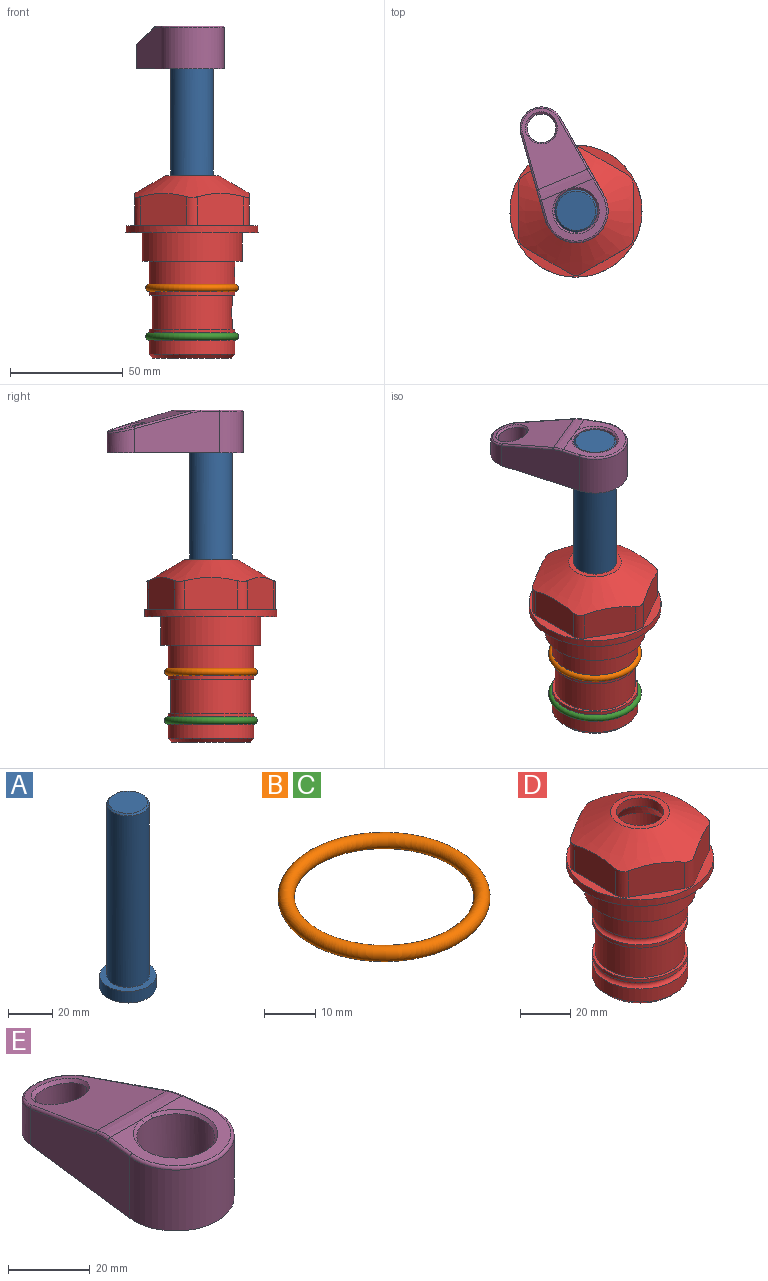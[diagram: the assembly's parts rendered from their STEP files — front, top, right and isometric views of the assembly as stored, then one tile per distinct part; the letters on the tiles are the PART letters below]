
ASSEMBLY  parts=5 mates=4
PART A: 6 faces, bbox 25.4x25.4x101.6 mm
  f0: plane 17.46x17.46mm, normal (0,0,1), area 239.5mm2, adj f5
  f1: plane 25.4x25.4mm, normal (0,0,-1), area 506.7mm2, adj f2
  f2: cylinder r=12.7mm len=25.4mm, axis (0,0,1), area 506.7mm2, adj f1,f3
  f3: plane 25.4x25.4mm, normal (0,0,1), area 221.7mm2, adj f2,f4
  f4: cylinder r=9.53mm len=94.46mm, axis (0,0,1), area 5653mm2, adj f3,f5
  f5: cone r=8.73mm half-angle=45deg, axis (0,0,-1), area 64.4mm2, adj f0,f4
PART B: 1 faces, bbox 44.7x44.7x3.2 mm
  f0: torus R=19.05mm, axis (0,0,1), area 1193.9mm2
PART C: same geometry as B
PART D: 36 faces, bbox 58.7x58.7x81 mm
  f0: cylinder r=17.78mm len=35.56mm, axis (0,0,1), area 1670.8mm2, adj f23,f24,f31
  f1: cylinder r=19.05mm len=38.1mm, axis (0,0,1), area 1191.9mm2, adj f26,f27,f30
  f2: plane 58.66x58.66mm, normal (0,0,-1), area 1150.6mm2, adj f3,f28
  f3: cylinder r=29.33mm len=58.66mm, axis (0,0,-1), area 585.1mm2, adj f2,f4
  f4: plane 58.66x58.66mm, normal (0,0,1), area 475.9mm2, adj f3,f5,f6,f7,f8,f9,f10,f11
  f5: plane 20.32x14.34mm, normal (-0.5,0.87,0), area 324.4mm2, adj f4,f15,f16,f17
  f6: plane 20.32x14.34mm, normal (0.5,0.87,0), area 324.4mm2, adj f4,f14,f15,f17
  f7: plane 23.48x14.34mm, normal (1,0,0), area 324.4mm2, adj f4,f13,f14,f17
  f8: plane 20.32x14.34mm, normal (0.5,-0.87,0), area 324.4mm2, adj f4,f12,f13,f17
  f9: plane 20.32x14.34mm, normal (-0.5,-0.87,0), area 324.4mm2, adj f4,f11,f12,f17
  f10: plane 23.48x14.34mm, normal (-1,0,0), area 324.4mm2, adj f4,f11,f16,f17
  f11: cylinder r=5.08mm len=12.85mm, axis (0,0,-1), area 67.2mm2, adj f4,f9,f10,f17
  f12: cylinder r=5.08mm len=12.85mm, axis (0,0,-1), area 67.2mm2, adj f4,f8,f9,f17
  f13: cylinder r=5.08mm len=12.85mm, axis (0,0,-1), area 67.2mm2, adj f4,f7,f8,f17
  f14: cylinder r=5.08mm len=12.85mm, axis (0,0,-1), area 67.2mm2, adj f4,f6,f7,f17
  f15: cylinder r=5.08mm len=12.85mm, axis (0,0,-1), area 67.2mm2, adj f4,f5,f6,f17
  f16: cylinder r=5.08mm len=12.85mm, axis (0,0,-1), area 67.2mm2, adj f4,f5,f10,f17
  f17: cone r=11.73mm half-angle=60deg, axis (0,0,-1), area 2071.8mm2, adj f5,f6,f7,f8,f9,f10,f11,f12
  f18: plane 23.46x23.46mm, normal (0,0,1), area 147.4mm2, adj f17,f35
  f19: plane 34.93x34.93mm, normal (0,0,-1), area 958mm2, adj f29
  f20: cylinder r=19.05mm len=38.1mm, axis (0,0,1), area 760.1mm2, adj f21,f29
  f21: torus R=19.05mm, axis (0,0,1), area 565.3mm2, adj f20,f22
  f22: cylinder r=19.05mm len=38.1mm, axis (0,0,1), area 190mm2, adj f21,f23
  f23: plane 38.1x38.1mm, normal (0,0,1), area 146.9mm2, adj f0,f22
  f24: plane 38.1x38.1mm, normal (0,0,-1), area 146.9mm2, adj f0,f25
  f25: cylinder r=19.05mm len=38.1mm, axis (0,0,1), area 190mm2, adj f24,f26
  f26: torus R=19.05mm, axis (0,0,1), area 565.3mm2, adj f1,f25
  f27: plane 44.45x44.45mm, normal (0,0,-1), area 411.7mm2, adj f1,f28
  f28: cylinder r=22.23mm len=44.45mm, axis (0,0,1), area 1773.5mm2, adj f2,f27
  f29: cone r=19.05mm half-angle=45deg, axis (0,0,1), area 257.5mm2, adj f19,f20
  f30: cylinder r=3.17mm len=6.75mm, axis (-1,0,0), area 128mm2, adj f1,f33
  f31: cylinder r=3.17mm len=6.35mm, axis (-1,0,0), area 102.5mm2, adj f0,f33
  f32: plane 25.4x25.4mm, normal (0,0,1), area 506.7mm2, adj f33
  f33: cylinder r=12.7mm len=66.42mm, axis (0,0,-1), area 5236.2mm2, adj f30,f31,f32,f34
  f34: cone r=9.53mm half-angle=30deg, axis (0,0,-1), area 443.4mm2, adj f33,f35
  f35: cylinder r=9.53mm len=19.05mm, axis (0,0,-1), area 240.9mm2, adj f18,f34
PART E: 31 faces, bbox 31.7x65.5x19.8 mm
  f0: plane 39.12x18.26mm, normal (0.99,0.12,0), area 612.2mm2, adj f1,f4,f7,f11,f13,f15
  f1: cylinder r=9.53mm len=18.91mm, axis (0,0,-1), area 296.1mm2, adj f0,f2,f7,f17
  f2: plane 39.12x18.26mm, normal (-0.99,0.12,0), area 612.2mm2, adj f1,f4,f7,f12,f14,f16
  f3: cylinder r=6.35mm len=12.7mm, axis (0,0,-1), area 362.4mm2, adj f7,f18
  f4: cylinder r=14.29mm len=28.58mm, axis (0,0,-1), area 882.2mm2, adj f0,f2,f7,f10
  f5: cylinder r=9.53mm len=19.05mm, axis (0,0,-1), area 1092.6mm2, adj f7,f19,f20
  f6: plane 26.99x23.69mm, normal (0,0,1), area 216.2mm2, adj f9,f10,f11,f12,f19
  f7: plane 63.5x28.58mm, normal (0,0,-1), area 661.8mm2, adj f0,f1,f2,f3,f4,f5,f22,f23
  f8: plane 33.52x23.6mm, normal (0,0.26,0.97), area 486mm2, adj f9,f15,f16,f17,f18
  f9: cylinder r=19.05mm len=24.72mm, axis (1,0,0), area 120.4mm2, adj f6,f8,f13,f14,f20
  f10: torus R=13.49mm, axis (0,0,1), area 59mm2, adj f4,f6,f11,f12
  f11: cylinder r=0.79mm len=8.67mm, axis (0.12,-0.99,0), area 10.8mm2, adj f0,f6,f10,f13
  f12: cylinder r=0.79mm len=8.67mm, axis (0.12,0.99,0), area 10.8mm2, adj f2,f6,f10,f14
  f13: bspline ~4.95x1.42mm, area 6.1mm2, adj f0,f9,f11,f15
  f14: bspline ~4.95x1.42mm, area 6.1mm2, adj f2,f9,f12,f16
  f15: cylinder r=0.79mm len=25.95mm, axis (0.12,-0.96,0.26), area 32.9mm2, adj f0,f8,f13,f17
  f16: cylinder r=0.79mm len=25.95mm, axis (0.12,0.96,-0.26), area 32.9mm2, adj f2,f8,f14,f17
  f17: bspline ~18.91x8.38mm, area 30mm2, adj f1,f8,f15,f16
  f18: bspline ~14.29x14.29mm, area 48.3mm2, adj f3,f8
  f19: cone r=9.53mm half-angle=45deg, axis (0,0,1), area 66.5mm2, adj f5,f6,f20
  f20: bspline ~3.22x0.96mm, area 3.5mm2, adj f5,f9,f19
  f21: plane 2.75x2.72mm, normal (0,0,-1), area 2.9mm2, adj f23,f25,f28
  f22: plane 23.05x15.88mm, normal (-0.99,-0.12,0), area 323.6mm2, adj f7,f25,f26,f27,f28,f29
  f23: plane 23.05x15.88mm, normal (0.99,-0.12,0), area 323.6mm2, adj f7,f21,f25,f27,f28,f30
  f24: cylinder r=9.53mm len=10.69mm, axis (0,0,-1), area 114.7mm2, adj f7,f27,f29,f30
  f25: cylinder r=12.7mm len=20.59mm, axis (0,0,-1), area 381.1mm2, adj f7,f21,f22,f23,f26,f28
  f26: plane 2.75x2.72mm, normal (0,0,-1), area 2.9mm2, adj f22,f25,f28
  f27: plane 19.72x18.37mm, normal (0,-0.26,-0.97), area 291.8mm2, adj f22,f23,f24,f28,f29,f30
  f28: cylinder r=15.88mm len=19.92mm, axis (1,0,0), area 54.8mm2, adj f21,f22,f23,f25,f26,f27
  f29: cylinder r=1.59mm len=11mm, axis (0,0,-1), area 34.7mm2, adj f7,f22,f24,f27
  f30: cylinder r=1.59mm len=11mm, axis (0,0,-1), area 34.7mm2, adj f7,f23,f24,f27
PLACE A rot(axis=(0,0,1),22.7deg) t=(0,0,27.55)mm
PLACE B at identity
PLACE C t=(0,0,-21.59)mm
PLACE D at identity fixed
PLACE E rot(axis=(0,0,1),22.7deg) t=(0,0,28.35)mm
MATE cylindrical D.f0 <-> A.f2  axis (0,0,1) through (0,0,-50.55)mm
MATE fastened C.f0 <-> D.f0  axis (0,0,1) through (0,0,-46.1)mm
MATE fastened B.f0 <-> D.f0  axis (0,0,1) through (0,0,-24.51)mm
MATE fastened A.f2 <-> E.f4  axis (0,0,1) through (0,0,91.05)mm
